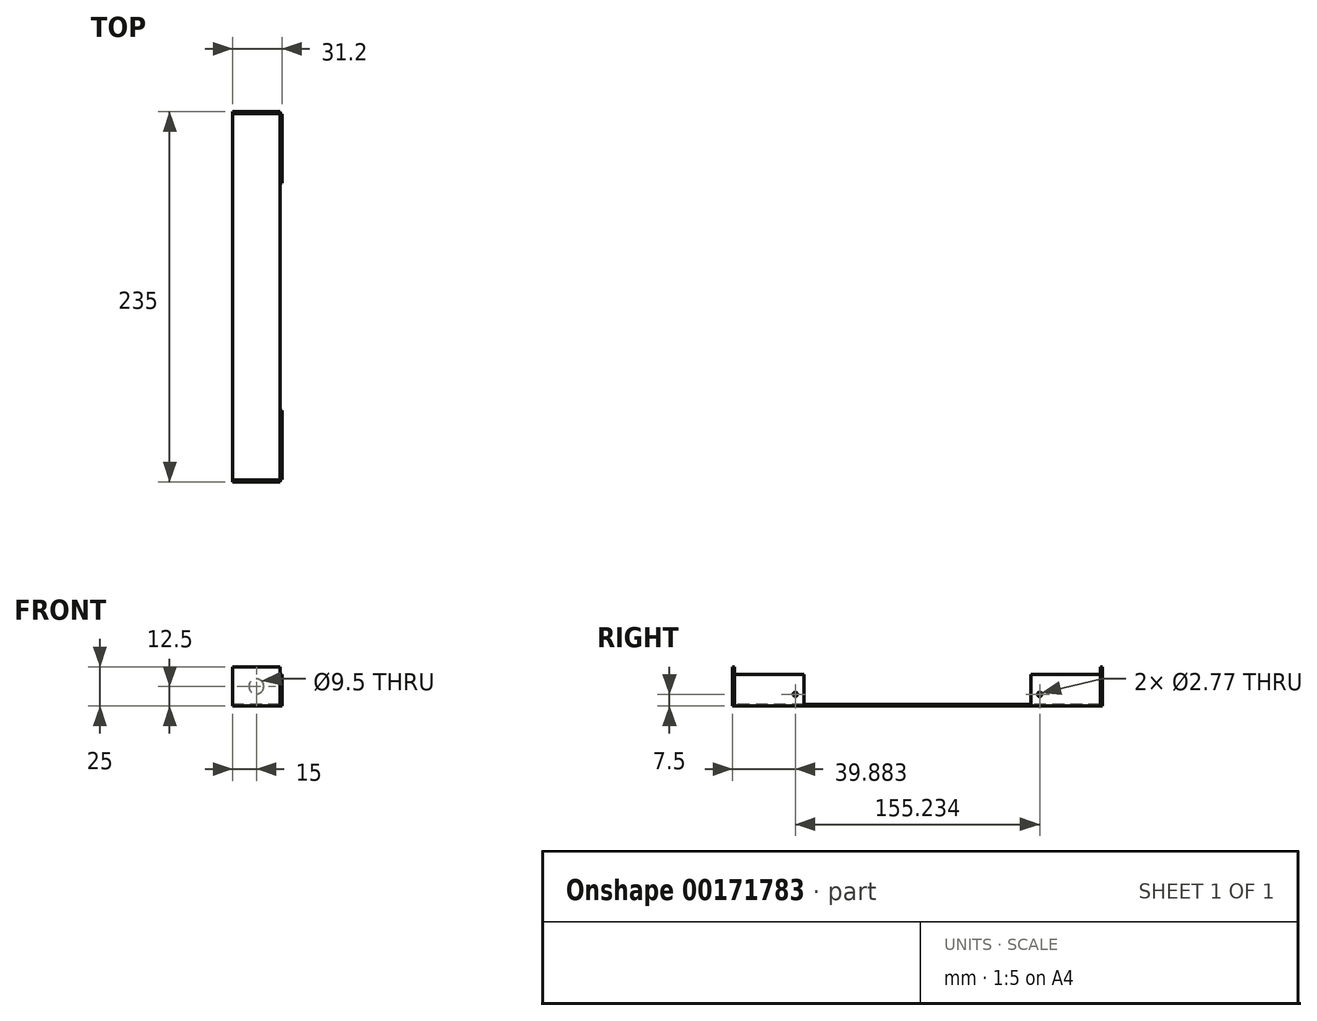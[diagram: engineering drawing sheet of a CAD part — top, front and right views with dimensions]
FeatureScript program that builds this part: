
annotation { "Feature Type Name" : "Feature", "Feature Type Description" : "" }
export const myFeature = defineFeature(function(context is Context, id is Id, definition is map)
    precondition{}
    {
        {
            var Q0;
            Q0=qCreatedBy(makeId("Right.planeOp"),FACE);
            var sketch = newSketch(context, id + "F0", { "sketchPlane" : qUnion([Q0])});
            skLineSegment(sketch, "E0.bottom", {"start": v(-117.5, 12.5) * mm, "end": v(-116.3, 12.5) * mm});
            skLineSegment(sketch, "E0.left", {"start": v(-117.5, 12.5) * mm, "end": v(-117.5, -12.5) * mm});
            skLineSegment(sketch, "E0.right", {"start": v(117.5, 12.5) * mm, "end": v(117.5, -12.5) * mm});
            skPoint(sketch, "E0.middle", {"position": v(0, 0) * mm});
            skLineSegment(sketch, "E1", {"start": v(-116.3, 12.5) * mm, "end": v(-116.3, -11.3) * mm});
            skLineSegment(sketch, "E2", {"start": v(-116.3, -11.3) * mm, "end": v(0, -11.29) * mm});
            skLineSegment(sketch, "E3.MirrorCS", {"start": v(116.3, -11.3) * mm, "end": v(0, -11.29) * mm});
            skLineSegment(sketch, "E4.MirrorCS", {"start": v(116.3, 12.5) * mm, "end": v(116.3, -11.3) * mm});
            skLineSegment(sketch, "E5.trimOffspring", {"start": v(116.3, 12.5) * mm, "end": v(117.5, 12.5) * mm});
            skPoint(sketch, "E6.end.orphan", {"position": v(0, -15) * mm});
            skLineSegment(sketch, "E7", {"start": v(-117.5, -12.5) * mm, "end": v(117.5, -12.5) * mm});
            skSolve(sketch);
        }
        {
            var Q0;
            Q0 = qSketchRegion(id + "F0", true);
            extrude(context, id + "F1", {"entities" : qUnion([Q0]), "endBound" : BoundingType.SYMMETRIC, "depth" : 30 * mm});
        }
        {
            var Q0;
            Q0=makeQuery(id+"F1.opExtrude","SWEPT_FACE",FACE,{"disambiguationData":[OSD([sQuery(id+"F0.wireOp",EDGE,"E0.right")])]});
            var sketch = newSketch(context, id + "F2", { "sketchPlane" : qUnion([Q0])});
            skCircle(sketch, "E8", {"center": v(0, 0) * mm, "radius": 4.75 * mm});
            skSolve(sketch);
        }
        {
            var Q0;
            Q0=makeQuery(id+"F1.opExtrude","CAP_FACE",FACE,{"disambiguationData":[OSD([sQuery(id+"F0.wireOp",EDGE,"E0.bottom"),sQuery(id+"F0.wireOp",EDGE,"E0.left"),sQuery(id+"F0.wireOp",EDGE,"E0.right"),sQuery(id+"F0.wireOp",EDGE,"E1"),sQuery(id+"F0.wireOp",EDGE,"E2"),sQuery(id+"F0.wireOp",EDGE,"E3.MirrorCS"),sQuery(id+"F0.wireOp",EDGE,"E4.MirrorCS"),sQuery(id+"F0.wireOp",EDGE,"E5.trimOffspring"),sQuery(id+"F0.wireOp",EDGE,"E7")])],"isStart":false});
            var sketch = newSketch(context, id + "F3", { "sketchPlane" : qUnion([Q0])});
            skLineSegment(sketch, "E9.bottom", {"start": v(-116.19, -12.5) * mm, "end": v(-72.2, -12.5) * mm});
            skLineSegment(sketch, "E9.top", {"start": v(-116.19, 7.5) * mm, "end": v(-72.2, 7.5) * mm});
            skLineSegment(sketch, "E9.left", {"start": v(-116.19, -12.5) * mm, "end": v(-116.19, 7.5) * mm});
            skLineSegment(sketch, "E10.MirrorCS", {"start": v(116.19, 7.5) * mm, "end": v(72.2, 7.5) * mm});
            skLineSegment(sketch, "E11.MirrorCS", {"start": v(116.19, -12.5) * mm, "end": v(116.19, 7.5) * mm});
            skLineSegment(sketch, "E12.MirrorCS", {"start": v(116.19, -12.5) * mm, "end": v(72.2, -12.5) * mm});
            skLineSegment(sketch, "E13.0", {"start": v(-72.2, -12.5) * mm, "end": v(-72.2, 7.5) * mm});
            skPoint(sketch, "E14.orphan", {"position": v(-71, 7.5) * mm});
            skPoint(sketch, "E15.orphan", {"position": v(-71, -12.5) * mm});
            skLineSegment(sketch, "E16.0", {"start": v(72.2, -12.5) * mm, "end": v(72.2, 7.5) * mm});
            skPoint(sketch, "E17.MirrorCS.end.orphan", {"position": v(71, 7.5) * mm});
            skPoint(sketch, "E17.MirrorCS.start.orphan", {"position": v(71, -12.5) * mm});
            skSolve(sketch);
        }
        {
            var Q0;
            Q0 = qSketchRegion(id + "F3", true);
            extrude(context, id + "F4", {"entities" : qUnion([Q0]), "operationType" : NewBodyOperationType.ADD, "depth" : 1.2 * mm});
        }
        {
            var Q0;
            Q0 = qSketchRegion(id + "F2", true);
            extrude(context, id + "F5", {"entities" : qUnion([Q0]), "operationType" : NewBodyOperationType.REMOVE, "endBound" : BoundingType.UP_TO_NEXT, "oppositeDirection" : true, "depth" : 25 * mm});
        }
        {
            var Q0;
            Q0=makeQuery(id+"F4.opExtrude","CAP_FACE",FACE,{"disambiguationData":[OSD([sQuery(id+"F3.wireOp",EDGE,"E9.bottom"),sQuery(id+"F3.wireOp",EDGE,"E9.top"),sQuery(id+"F3.wireOp",EDGE,"E9.left"),sQuery(id+"F3.wireOp",EDGE,"E9.right")])],"isStart":false});
            var sketch = newSketch(context, id + "F6", { "sketchPlane" : qUnion([Q0])});
            skCircle(sketch, "E18", {"center": v(-77.62, -5) * mm, "radius": 1.39 * mm});
            skCircle(sketch, "E19.MirrorC", {"center": v(77.62, -5) * mm, "radius": 1.39 * mm});
            skSolve(sketch);
        }
        {
            var Q0;
            Q0 = qSketchRegion(id + "F6", true);
            extrude(context, id + "F7", {"entities" : qUnion([Q0]), "operationType" : NewBodyOperationType.REMOVE, "endBound" : BoundingType.UP_TO_NEXT, "oppositeDirection" : true, "depth" : 25 * mm});
        }
    });
